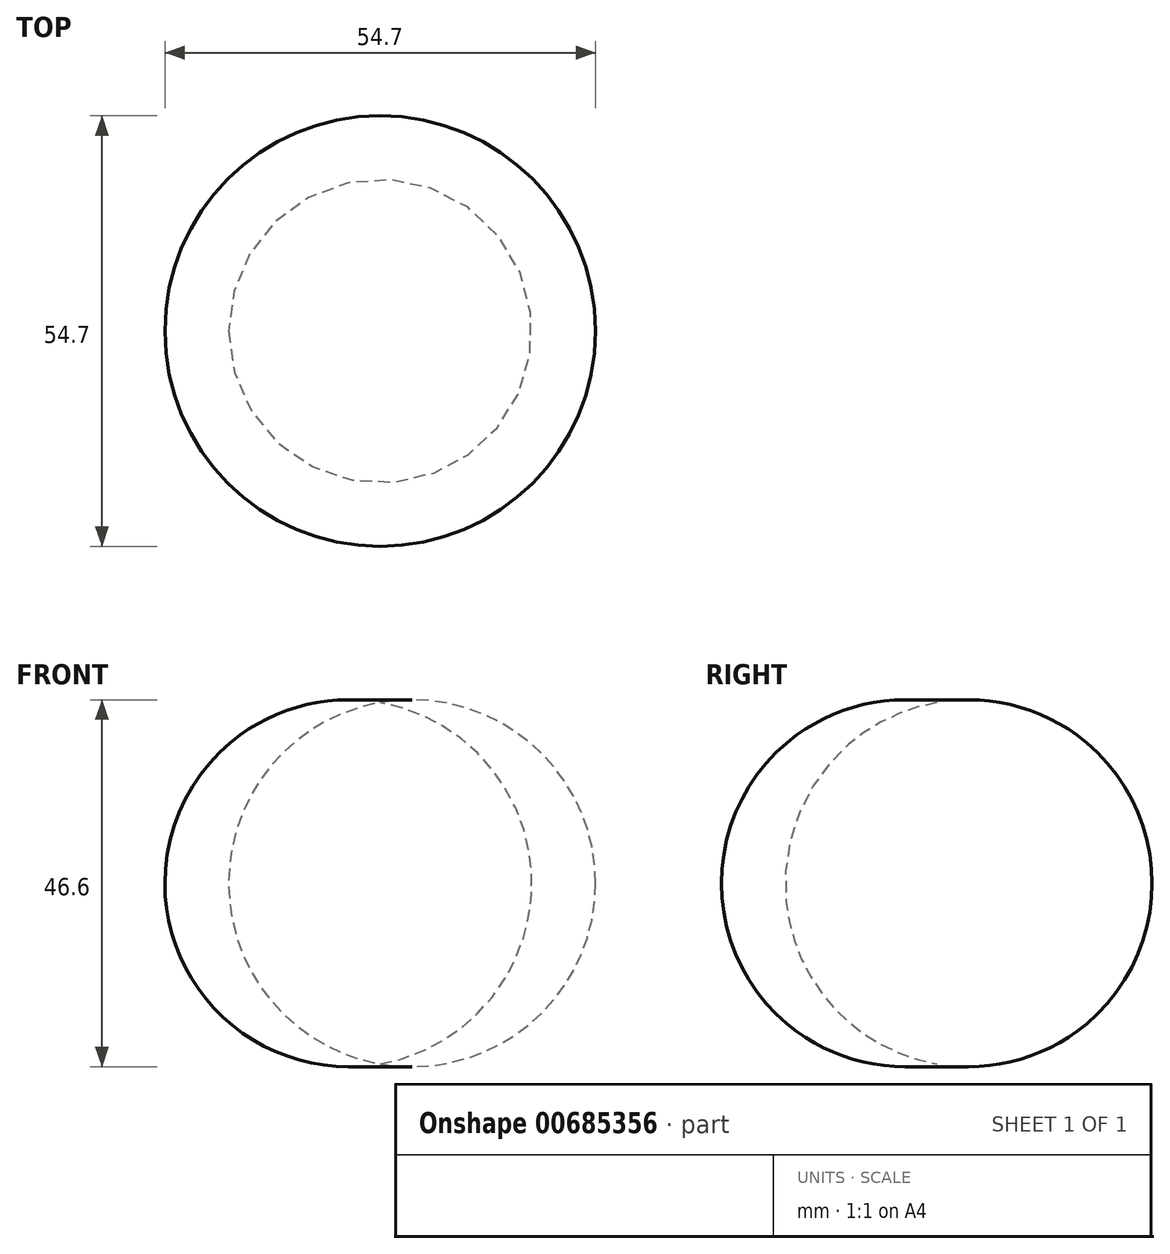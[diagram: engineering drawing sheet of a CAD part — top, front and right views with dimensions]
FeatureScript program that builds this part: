
annotation { "Feature Type Name" : "Feature", "Feature Type Description" : "" }
export const myFeature = defineFeature(function(context is Context, id is Id, definition is map)
    precondition{}
    {
        {
            var Q0;
            Q0=qCreatedBy(makeId("Front.planeOp"),FACE);
            var sketch = newSketch(context, id + "F0", { "sketchPlane" : qUnion([Q0])});
            skArc(sketch, "E0", {"start": v(0, 45.9) * mm, "mid": v(-19.26, 22.95) * mm, "end": v(0, 0) * mm});
            skLineSegment(sketch, "E1", {"start": v(0, 0) * mm, "end": v(0, 45.9) * mm});
            skSolve(sketch);
        }
        {
            var Q0;
            Q0=sQuery(id+"F0.wireOp",EDGE,"E0");
            var Q1;
            Q1=sQuery(id+"F0.wireOp",EDGE,"E1");
            revolve(context, id + "F1", {"bodyType" : ToolBodyType.SURFACE, "surfaceEntities" : qUnion([Q0]), "axis" : qUnion([Q1]), "revolveType" : RevolveType.FULL});
        }
    });
